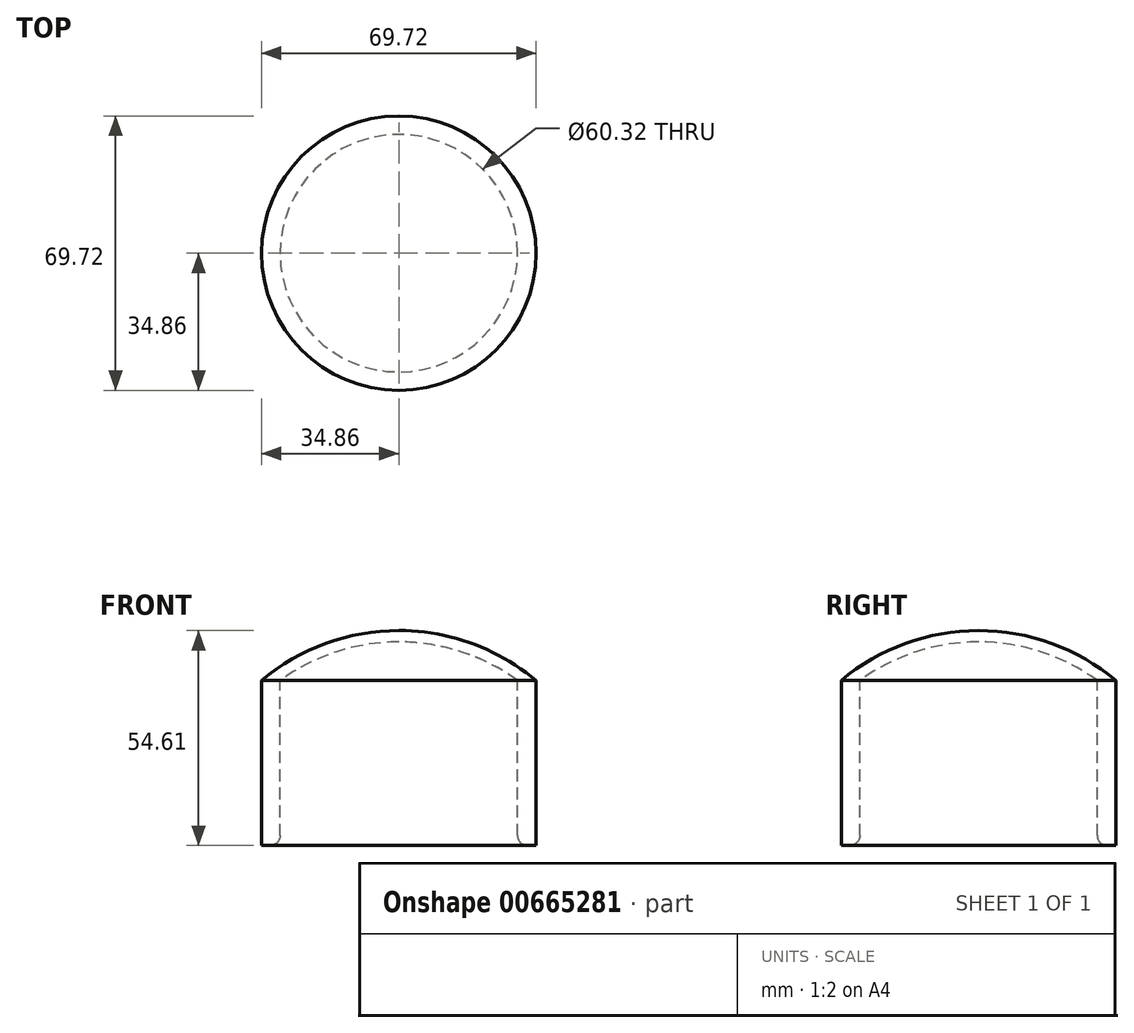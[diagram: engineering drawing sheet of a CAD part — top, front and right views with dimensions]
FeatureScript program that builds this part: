
annotation { "Feature Type Name" : "Feature", "Feature Type Description" : "" }
export const myFeature = defineFeature(function(context is Context, id is Id, definition is map)
    precondition{}
    {
        {
            var Q0;
            Q0=qCreatedBy(makeId("Front.planeOp"),FACE);
            var sketch = newSketch(context, id + "F0", { "sketchPlane" : qUnion([Q0])});
            skLineSegment(sketch, "E0", {"start": v(0, 133.2) * mm, "end": v(0, -97.05) * mm, "construction": true});
            skLineSegment(sketch, "E1.bottom", {"start": v(30.16, 0) * mm, "end": v(34.86, 0) * mm});
            skLineSegment(sketch, "E1.top", {"start": v(30.16, 41.91) * mm, "end": v(34.86, 41.91) * mm});
            skLineSegment(sketch, "E1.left", {"start": v(30.16, 0) * mm, "end": v(30.16, 41.9) * mm});
            skLineSegment(sketch, "E1.right", {"start": v(34.86, 0) * mm, "end": v(34.86, 41.9) * mm});
            skArc(sketch, "E2", {"start": v(34.86, 41.9) * mm, "mid": v(18.55, 51.34) * mm, "end": v(0, 54.6) * mm});
            skPoint(sketch, "E3", {"position": v(0, 54.6) * mm});
            skPoint(sketch, "E4", {"position": v(0, -53.78) * mm});
            skArc(sketch, "E5", {"start": v(30.16, 41.9) * mm, "mid": v(15.86, 49.2) * mm, "end": v(0, 51.71) * mm});
            skLineSegment(sketch, "E6", {"start": v(0, 54.6) * mm, "end": v(0, 51.71) * mm});
            skSolve(sketch);
        }
        {
            var Q0;
            Q0=makeQuery(id+"F0.imprint","IMPRINT",FACE,{"disambiguationData":[TD([[makeQuery(id+"F0.imprint","IMPRINT",EDGE,{"derivedFrom":sQuery(id+"F0.wireOp",EDGE,"E1.top")}),1.0]])]});
            var Q1;
            Q1=makeQuery(id+"F0.imprint","IMPRINT",FACE,{"disambiguationData":[TD([[makeQuery(id+"F0.imprint","IMPRINT",EDGE,{"derivedFrom":sQuery(id+"F0.wireOp",EDGE,"E1.bottom")}),1.0]])]});
            var Q2;
            Q2=sQuery(id+"F0.wireOp",EDGE,"E0");
            revolve(context, id + "F1", {"entities" : qUnion([Q0, Q1]), "axis" : qUnion([Q2]), "revolveType" : RevolveType.FULL});
        }
        {
            var Q0;
            Q0=makeQuery(id+"F1.opRevolve","SWEPT_EDGE",EDGE,{"disambiguationData":[OSD([sQuery(id+"F0.wireOp",EDGE,"E1.bottom"),sQuery(id+"F0.wireOp",EDGE,"E1.left")])]});
            fillet(context, id + "F2", {"entities" : qUnion([Q0]), "radius" : 2.54 * mm, "tangentPropagation" : true, "allowEdgeOverflow" : false});
        }
    });
